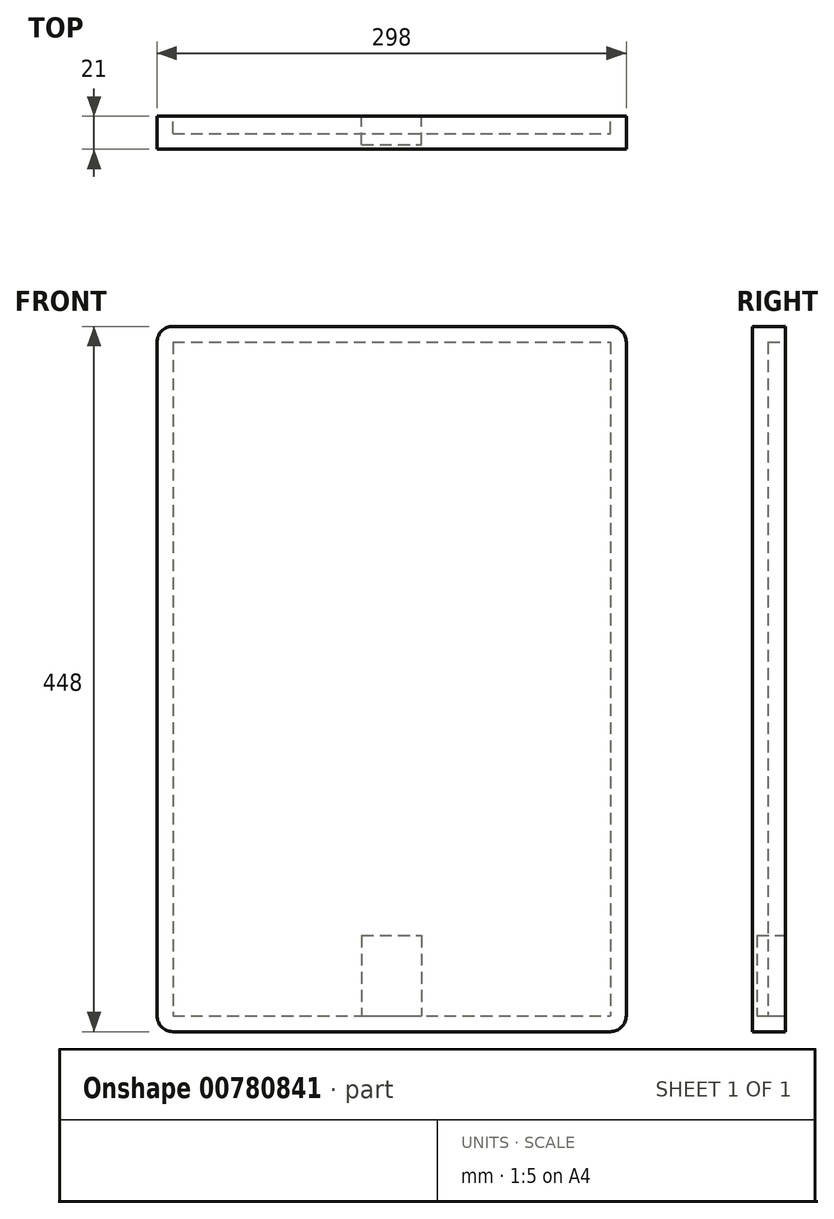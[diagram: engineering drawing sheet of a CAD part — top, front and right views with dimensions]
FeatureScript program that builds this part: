
annotation { "Feature Type Name" : "Feature", "Feature Type Description" : "" }
export const myFeature = defineFeature(function(context is Context, id is Id, definition is map)
    precondition{}
    {
        {
            var Q0;
            Q0=qCreatedBy(makeId("Front.planeOp"),FACE);
            var sketch = newSketch(context, id + "F0", { "sketchPlane" : qUnion([Q0])});
            skLineSegment(sketch, "E0.bottom", {"start": v(-139, 224) * mm, "end": v(139, 224) * mm});
            skLineSegment(sketch, "E0.top", {"start": v(-139, -224) * mm, "end": v(139, -224) * mm});
            skLineSegment(sketch, "E0.left", {"start": v(-149, 214) * mm, "end": v(-149, -214) * mm});
            skLineSegment(sketch, "E0.right", {"start": v(149, 214) * mm, "end": v(149, -214) * mm});
            skPoint(sketch, "E0.middle", {"position": v(0, 0) * mm});
            skLineSegment(sketch, "E1.bottom", {"start": v(-19, -163) * mm, "end": v(19, -163) * mm});
            skLineSegment(sketch, "E1.top", {"start": v(-19, -214) * mm, "end": v(19, -214) * mm});
            skLineSegment(sketch, "E1.left", {"start": v(-19, -163) * mm, "end": v(-19, -214) * mm});
            skLineSegment(sketch, "E1.right", {"start": v(19, -163) * mm, "end": v(19, -214) * mm});
            skPoint(sketch, "E2.visualSharp", {"position": v(-149, 224) * mm});
            skArc(sketch, "E2.filletArc", {"start": v(-139, 224) * mm, "mid": v(-146.07, 221.07) * mm, "end": v(-149, 214) * mm});
            skPoint(sketch, "E3.visualSharp", {"position": v(149, 224) * mm});
            skArc(sketch, "E3.filletArc", {"start": v(149, 214) * mm, "mid": v(146.07, 221.07) * mm, "end": v(139, 224) * mm});
            skPoint(sketch, "E4.visualSharp", {"position": v(149, -224) * mm});
            skArc(sketch, "E4.filletArc", {"start": v(139, -224) * mm, "mid": v(146.07, -221.07) * mm, "end": v(149, -214) * mm});
            skPoint(sketch, "E5.visualSharp", {"position": v(-149, -224) * mm});
            skArc(sketch, "E5.filletArc", {"start": v(-149, -214) * mm, "mid": v(-146.07, -221.07) * mm, "end": v(-139, -224) * mm});
            skSolve(sketch);
        }
        {
            var Q0;
            Q0=makeQuery(id+"F0.imprint","IMPRINT",FACE,{"disambiguationData":[TD([[makeQuery(id+"F0.imprint","IMPRINT",EDGE,{"derivedFrom":sQuery(id+"F0.wireOp",EDGE,"E1.bottom")}),-1.0]])]});
            var Q1;
            Q1=makeQuery(id+"F0.imprint","IMPRINT",FACE,{"disambiguationData":[TD([[makeQuery(id+"F0.imprint","IMPRINT",EDGE,{"derivedFrom":sQuery(id+"F0.wireOp",EDGE,"E0.bottom")}),-1.0]])]});
            extrude(context, id + "F1", {"entities" : qUnion([Q0, Q1]), "depth" : 21 * mm, "offsetDistance" : 25 * mm});
        }
        {
            var Q0;
            Q0=makeQuery(id+"F0.imprint","IMPRINT",FACE,{"disambiguationData":[TD([[makeQuery(id+"F0.imprint","IMPRINT",EDGE,{"derivedFrom":sQuery(id+"F0.wireOp",EDGE,"E1.bottom")}),-1.0]])]});
            extrude(context, id + "F2", {"entities" : qUnion([Q0]), "depth" : 18 * mm, "offsetDistance" : 25 * mm});
        }
        {
            var Q0;
            Q0=makeQuery(id+"F1.opExtrude","CAP_FACE",FACE,{"disambiguationData":[OSD([sQuery(id+"F0.wireOp",EDGE,"E0.bottom"),sQuery(id+"F0.wireOp",EDGE,"E0.top"),sQuery(id+"F0.wireOp",EDGE,"E0.left"),sQuery(id+"F0.wireOp",EDGE,"E0.right"),sQuery(id+"F0.wireOp",EDGE,"E2.filletArc"),sQuery(id+"F0.wireOp",EDGE,"E3.filletArc"),sQuery(id+"F0.wireOp",EDGE,"E4.filletArc"),sQuery(id+"F0.wireOp",EDGE,"E5.filletArc")])],"isStart":true});
            shell(context, id + "F3", {"entities" : qUnion([Q0]), "thickness" : 10 * mm});
        }
    });
